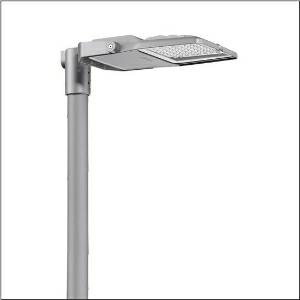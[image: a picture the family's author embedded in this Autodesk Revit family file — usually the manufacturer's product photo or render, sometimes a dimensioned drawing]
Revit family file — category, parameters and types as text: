
# Revit family: floodlight_fl_21_iq_mini___pl33t_5xa7771b2f3a_2789
name_source: partatom
category: Lighting Fixtures
units: mm (PartAtom-declared; Revit-internal decimal feet)

## family parameters
Cut with Voids When Loaded = No
Host = Face
Light Source = No
Part Type = Normal
Room Calculation Point = No
Round Connector Dimension = Use Diameter
Shared = No

## types (1)
- --- (1 x LED, 6170 lm, 45.5 W, 3000K)
    Apparent Load = 46 VA
    CIE Flux Codes = 26 75 99 100 100
    Color Rendering = 70
    Color Temperature = 3000K
    Default Elevation = 1800 mm
    Description = Floodlight FL 21 iQ mini, floodlight, primary light control with lens, of PMMA, primary optical cover: protective disc, of toughened safety glass, transparent, light distribution: PL33T, light emission: direct distribution, installation type: surface-mounted, LED, High Power LED, rated luminous flux: 6.170lm, luminous efficacy: 136lm/W, light colour: 730, colour temperature: 3000K, control gear: iQ Comfort/DALI, control: Auto-Match, Temp-Guard, Lumen-Switch, Night-Set, Smart-Wire, Light-Fading, Desk-Remote (wireless, voltage-free reading and setting of iQ features in the workshop via application-optimized NFC function/RFID function), optimised constant luminous flux control (CLO 2.0), with terminal, 6-pole, mains connection: 220..240V, AC, 50/60Hz, start of lifetime: 46W, end of service life: 48W, reduction: 22W, luminaire housing, of diecast aluminium, powder-coated, Siteco® metallic grey (DB 702S), corrosivity category C5 mid according to DIN EN ISO 12944, suitable for swimming pools, chlorine-resistant, sealing non-destructively replaceable, please order mast flange separately, mast bracket, of steel, galvanised, powder-coated, Siteco® metallic grey (DB 702S), protection rating (complete): IP66, insulation class (complete): insulation class II (safety insulation), certification: CE, ENEC, VDE, protection symbol: D, impact resistance: IK08, permissible operating ambient temperature: -40..+40°C, permissible operating ambient temperature for outdoor applications: -40..+50°C, standard: DIN EN 12944, LABS conformity tested according to VDMA 24364:2018-05, packaging unit: 1 piece

Light Distribution: PL33T
    Height = 70 mm
    Lamp = 1 x LED
    Lamp Light Flux = 6170 lm
    Lamp Power = 45.5 W
    Lamp count = 1
    Length = 485 mm
    Luminous efficacy = 136 lm/W
    Manufacturer = Siteco
    ModVariant = No
    Model = 5XA7771B2F3A
    Number of Poles = 1
    OnlyDefault = Yes
    Power Factor = 1
    Product Name = Floodlight FL 21 iQ mini | PL33T
    Product group = floodlight | pylon annexe
    ProductGroupID = 6201
    Protection Class = Protection class II
    Protection Degree = IP 66
    RLX_Detail_Level = 1
    RLX_Emergency_Light_Flux = 0 lm
    RLX_Emergency_Type = 0
    RLX_Emergency_Type_DB = No
    RlxData = <blob elided: 101117 chars, md5=102a1aa0>
    Socket = socket
    Standby Power = 0 W
    System Light Flux = 6170 lm
    System Power = 46 W
    Type Comments = factory setting: luminous flux: 100 % | dim-lin: 254 | 463 mA
    Type Image = l_1007125.jpg
    URL = http://relux.com
    VarID = @adj_171725
    Voltage = 0 V
    Weight = 0.00 kg
    Width = 337 mm

## geometry (parser evidence)
native form markers: Blend x4, Sweep x11
no freeform markers — native parametric forms only
